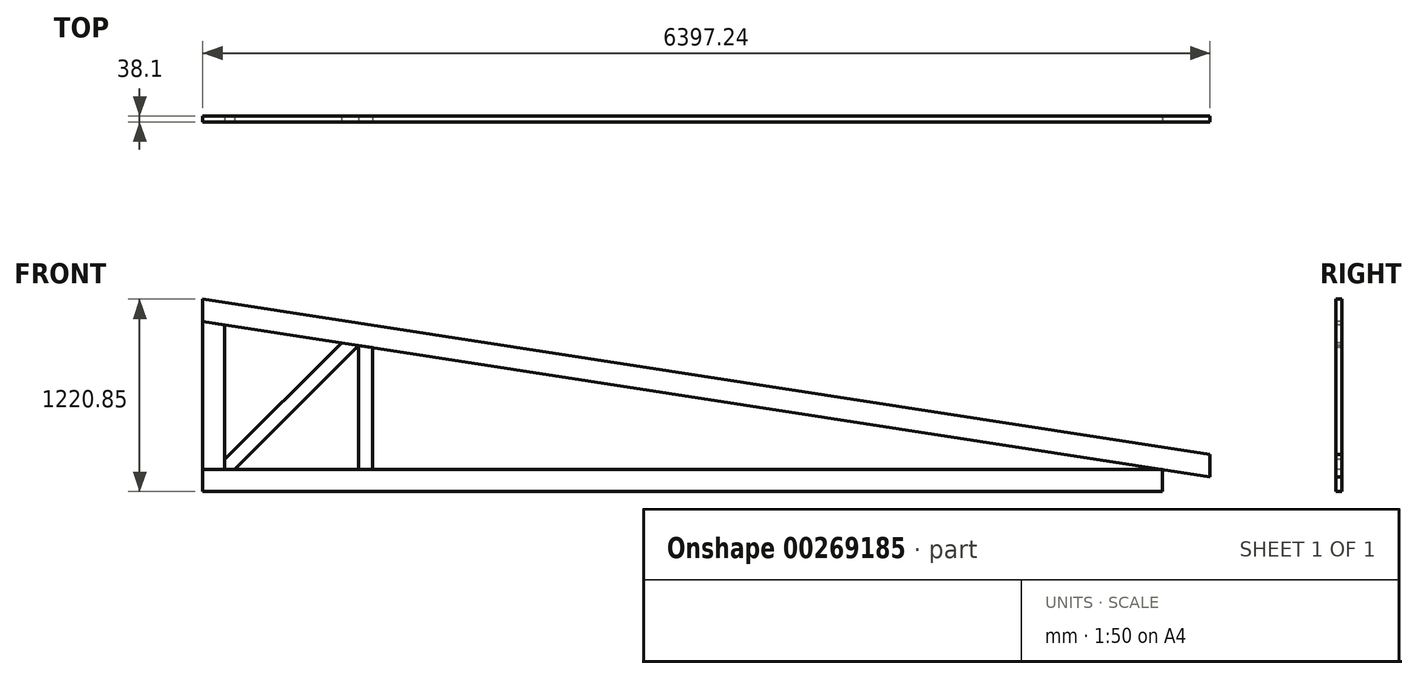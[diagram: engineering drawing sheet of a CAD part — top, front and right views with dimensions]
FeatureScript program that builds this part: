
annotation { "Feature Type Name" : "Feature", "Feature Type Description" : "" }
export const myFeature = defineFeature(function(context is Context, id is Id, definition is map)
    precondition{}
    {
        {
            var Q0;
            Q0=qCreatedBy(makeId("Front.planeOp"),FACE);
            var sketch = newSketch(context, id + "F0", { "sketchPlane" : qUnion([Q0])});
            skLineSegment(sketch, "E0.bottom", {"start": v(0, 0) * mm, "end": v(139.7, 0) * mm});
            skLineSegment(sketch, "E0.top", {"start": v(0, 939.8) * mm, "end": v(139.7, 939.8) * mm});
            skLineSegment(sketch, "E0.left", {"start": v(0, 0) * mm, "end": v(0, 939.8) * mm});
            skLineSegment(sketch, "E0.right", {"start": v(139.7, 0) * mm, "end": v(139.7, 939.8) * mm});
            skSolve(sketch);
        }
        {
            var Q0;
            Q0 = qSketchRegion(id + "F0", true);
            extrude(context, id + "F1", {"entities" : qUnion([Q0]), "oppositeDirection" : true, "depth" : 38.1 * mm});
        }
        {
            var Q0;
            Q0=makeQuery(id+"F1.opExtrude","CAP_FACE",FACE,{"disambiguationData":[OSD([sQuery(id+"F0.wireOp",EDGE,"E0.bottom"),sQuery(id+"F0.wireOp",EDGE,"E0.top"),sQuery(id+"F0.wireOp",EDGE,"E0.left"),sQuery(id+"F0.wireOp",EDGE,"E0.right")])],"isStart":true});
            var sketch = newSketch(context, id + "F2", { "sketchPlane" : qUnion([Q0])});
            skLineSegment(sketch, "E1.bottom", {"start": v(0, 0) * mm, "end": v(6096, 0) * mm});
            skLineSegment(sketch, "E1.top", {"start": v(0, -139.7) * mm, "end": v(6096, -139.7) * mm});
            skLineSegment(sketch, "E1.left", {"start": v(0, 0) * mm, "end": v(0, -139.7) * mm});
            skLineSegment(sketch, "E1.right", {"start": v(6096, 0) * mm, "end": v(6096, -139.7) * mm});
            skSolve(sketch);
        }
        {
            var Q0;
            Q0 = qSketchRegion(id + "F2", true);
            var Q1;
            Q1=makeQuery(id+"F1.opExtrude","CAP_FACE",FACE,{"disambiguationData":[OSD([sQuery(id+"F0.wireOp",EDGE,"E0.bottom"),sQuery(id+"F0.wireOp",EDGE,"E0.top"),sQuery(id+"F0.wireOp",EDGE,"E0.left"),sQuery(id+"F0.wireOp",EDGE,"E0.right")])],"isStart":false});
            extrude(context, id + "F3", {"entities" : qUnion([Q0]), "endBound" : BoundingType.UP_TO_SURFACE, "oppositeDirection" : true, "endBoundEntityFace" : qUnion([Q1]), "depth" : 25.4 * mm});
        }
        {
            var Q0;
            Q0=makeQuery(id+"F3.boolean.opBoolean","MERGE",FACE,{"derivedFrom":[makeQuery(id+"F1.opExtrude","CAP_FACE",FACE,{"disambiguationData":[OSD([sQuery(id+"F0.wireOp",EDGE,"E0.bottom"),sQuery(id+"F0.wireOp",EDGE,"E0.top"),sQuery(id+"F0.wireOp",EDGE,"E0.left"),sQuery(id+"F0.wireOp",EDGE,"E0.right")])],"isStart":true}),makeQuery(id+"F3.opExtrude","CAP_FACE",FACE,{"disambiguationData":[OSD([sQuery(id+"F2.wireOp",EDGE,"E1.bottom"),sQuery(id+"F2.wireOp",EDGE,"E1.top"),sQuery(id+"F2.wireOp",EDGE,"E1.left"),sQuery(id+"F2.wireOp",EDGE,"E1.right")])],"isStart":true})]});
            var sketch = newSketch(context, id + "F4", { "sketchPlane" : qUnion([Q0])});
            skLineSegment(sketch, "E2", {"start": v(0, 939.8) * mm, "end": v(139.7, 918.26) * mm});
            skLineSegment(sketch, "E3", {"start": v(0, 939.8) * mm, "end": v(139.7, 939.8) * mm});
            skLineSegment(sketch, "E4", {"start": v(139.7, 939.8) * mm, "end": v(139.7, 918.26) * mm});
            skSolve(sketch);
        }
        {
            var Q0;
            Q0 = qSketchRegion(id + "F4", true);
            extrude(context, id + "F5", {"entities" : qUnion([Q0]), "operationType" : NewBodyOperationType.REMOVE, "endBound" : BoundingType.THROUGH_ALL, "oppositeDirection" : true, "depth" : 25.4 * mm});
        }
        {
            var Q0;
            Q0=makeQuery(id+"F3.boolean.opBoolean","MERGE",FACE,{"derivedFrom":[makeQuery(id+"F1.opExtrude","CAP_FACE",FACE,{"disambiguationData":[OSD([sQuery(id+"F0.wireOp",EDGE,"E0.bottom"),sQuery(id+"F0.wireOp",EDGE,"E0.top"),sQuery(id+"F0.wireOp",EDGE,"E0.left"),sQuery(id+"F0.wireOp",EDGE,"E0.right")])],"isStart":true}),makeQuery(id+"F3.opExtrude","CAP_FACE",FACE,{"disambiguationData":[OSD([sQuery(id+"F2.wireOp",EDGE,"E1.bottom"),sQuery(id+"F2.wireOp",EDGE,"E1.top"),sQuery(id+"F2.wireOp",EDGE,"E1.left"),sQuery(id+"F2.wireOp",EDGE,"E1.right")])],"isStart":true})]});
            var sketch = newSketch(context, id + "F6", { "sketchPlane" : qUnion([Q0])});
            skLineSegment(sketch, "E5", {"start": v(0, 939.8) * mm, "end": v(6096, 0) * mm});
            skLineSegment(sketch, "E6", {"start": v(6096, 0) * mm, "end": v(6397.24, -46.44) * mm});
            skLineSegment(sketch, "E7", {"start": v(6397.24, 94.9) * mm, "end": v(0, 1081.15) * mm});
            skLineSegment(sketch, "E8", {"start": v(0, 939.8) * mm, "end": v(0, 1081.15) * mm});
            skLineSegment(sketch, "E9", {"start": v(6397.24, -46.44) * mm, "end": v(6397.24, 94.9) * mm});
            skSolve(sketch);
        }
        {
            var Q0;
            Q0 = qSketchRegion(id + "F6", true);
            extrude(context, id + "F7", {"entities" : qUnion([Q0]), "oppositeDirection" : true, "depth" : 38.1 * mm});
        }
        {
            var Q0;
            Q0=makeQuery(id+"F1.opExtrude","CAP_FACE",FACE,{"disambiguationData":[OSD([sQuery(id+"F0.wireOp",EDGE,"E0.bottom"),sQuery(id+"F0.wireOp",EDGE,"E0.top"),sQuery(id+"F0.wireOp",EDGE,"E0.left"),sQuery(id+"F0.wireOp",EDGE,"E0.right")])],"isStart":true});
            var sketch = newSketch(context, id + "F8", { "sketchPlane" : qUnion([Q0])});
            skLineSegment(sketch, "E10.0", {"start": v(202.56, 0) * mm, "end": v(989.77, 787.21) * mm});
            skLineSegment(sketch, "E11.0", {"start": v(139.7, 62.86) * mm, "end": v(880.84, 804) * mm});
            skLineSegment(sketch, "E12", {"start": v(139.7, 0) * mm, "end": v(139.7, 62.86) * mm});
            skLineSegment(sketch, "E13", {"start": v(139.7, 0) * mm, "end": v(202.56, 0) * mm});
            skLineSegment(sketch, "E14.0", {"start": v(880.84, 804) * mm, "end": v(989.77, 787.21) * mm});
            skPoint(sketch, "E15.orphan", {"position": v(6397.24, -46.44) * mm});
            skPoint(sketch, "E16.orphan", {"position": v(0, 939.8) * mm});
            skSolve(sketch);
        }
        {
            var Q0;
            Q0 = qSketchRegion(id + "F8", true);
            extrude(context, id + "F9", {"entities" : qUnion([Q0]), "oppositeDirection" : true, "depth" : 38.1 * mm});
        }
        {
            var Q0;
            Q0=makeQuery(id+"F9.opExtrude","CAP_FACE",FACE,{"disambiguationData":[OSD([sQuery(id+"F8.wireOp",EDGE,"E10.0"),sQuery(id+"F8.wireOp",EDGE,"E11.0"),sQuery(id+"F8.wireOp",EDGE,"E12"),sQuery(id+"F8.wireOp",EDGE,"E13"),sQuery(id+"F8.wireOp",EDGE,"E14.0")])],"isStart":true});
            var sketch = newSketch(context, id + "F10", { "sketchPlane" : qUnion([Q0])});
            skLineSegment(sketch, "E17", {"start": v(989.77, 787.21) * mm, "end": v(989.77, 0) * mm});
            skLineSegment(sketch, "E18", {"start": v(989.77, 0) * mm, "end": v(1078.67, 0) * mm});
            skLineSegment(sketch, "E19", {"start": v(1078.67, 0) * mm, "end": v(1078.67, 773.5) * mm});
            skLineSegment(sketch, "E20.0", {"start": v(989.77, 787.21) * mm, "end": v(1078.67, 773.5) * mm});
            skPoint(sketch, "E21.orphan", {"position": v(6397.24, -46.44) * mm});
            skPoint(sketch, "E22.orphan", {"position": v(0, 939.8) * mm});
            skSolve(sketch);
        }
        {
            var Q0;
            Q0 = qSketchRegion(id + "F10", true);
            extrude(context, id + "F11", {"entities" : qUnion([Q0]), "oppositeDirection" : true, "depth" : 38.1 * mm});
        }
    });
